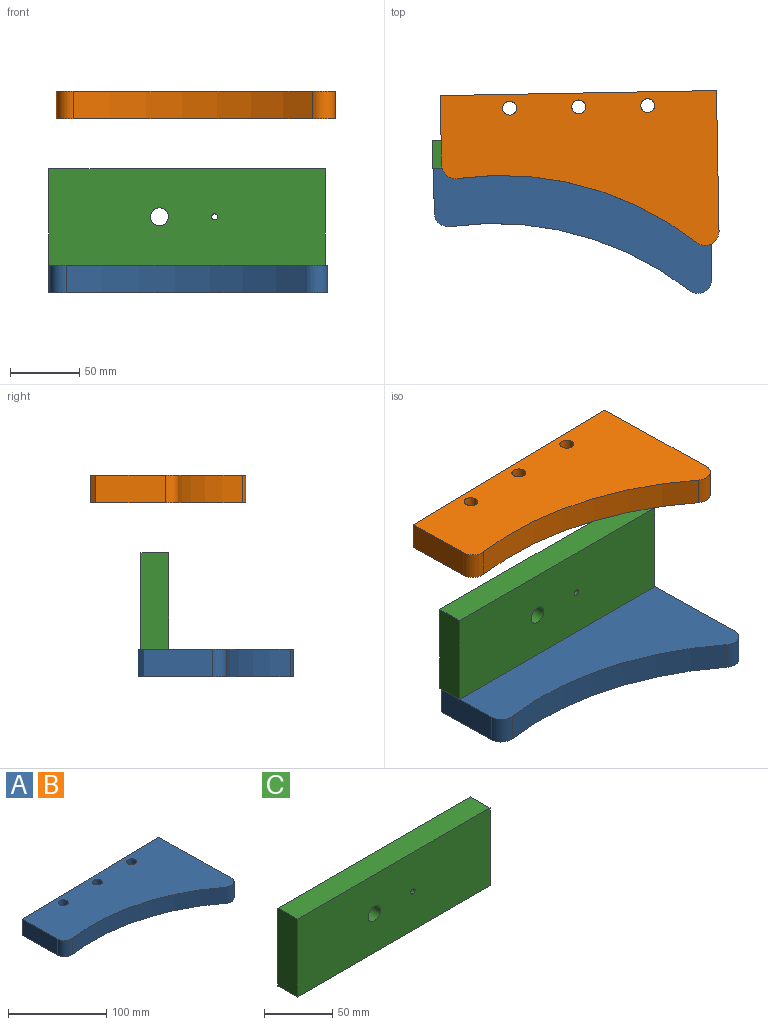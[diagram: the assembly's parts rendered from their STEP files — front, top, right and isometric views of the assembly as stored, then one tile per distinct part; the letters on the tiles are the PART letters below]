
ASSEMBLY  parts=3 mates=1
PART A: 11 faces, bbox 201.8x112.1x20 mm
  f0: plane 101.93x20mm, normal (1,0.02,0), area 2039mm2, adj f1,f7,f9,f10
  f1: plane 199.97x20mm, normal (-0.02,1,0), area 4000mm2, adj f0,f2,f9,f10
  f2: plane 50.28x20mm, normal (-1,-0.02,0), area 1005.8mm2, adj f1,f3,f9,f10
  f3: cylinder r=10mm len=20mm, axis (0,0,-1), area 338.6mm2, adj f2,f4,f9,f10
  f4: cylinder r=229.46mm len=173.36mm, axis (0,0,-1), area 3687.3mm2, adj f3,f7,f9,f10
  f5: cylinder r=5mm len=20mm, axis (0,0,-1), area 628.3mm2, adj f9,f10
  f6: cylinder r=5mm len=20mm, axis (0,0,-1), area 628.3mm2, adj f9,f10
  f7: cylinder r=10mm len=20mm, axis (0,0,-1), area 450.4mm2, adj f0,f4,f9,f10
  f8: cylinder r=5mm len=20mm, axis (0,0,-1), area 628.3mm2, adj f9,f10
  f9: plane 201.84x112.12mm, normal (0,0,1), area 14669.9mm2, adj f0,f1,f2,f3,f4,f5,f6,f7
  f10: plane 201.84x112.12mm, normal (0,0,-1), area 14669.9mm2, adj f0,f1,f2,f3,f4,f5,f6,f7
PART B: same geometry as A
PART C: 8 faces, bbox 200x20x70 mm
  f0: plane 200x20mm, normal (0,0,1), area 4000mm2, adj f1,f5,f6,f7
  f1: plane 70x20mm, normal (-1,0,0), area 1400mm2, adj f0,f2,f6,f7
  f2: plane 200x20mm, normal (0,0,-1), area 4000mm2, adj f1,f5,f6,f7
  f3: cylinder r=6.5mm len=20mm, axis (0,1,0), area 816.8mm2, adj f6,f7
  f4: cylinder r=2.25mm len=20mm, axis (0,1,0), area 282.7mm2, adj f6,f7
  f5: plane 70x20mm, normal (1,0,0), area 1400mm2, adj f0,f2,f6,f7
  f6: plane 200x70mm, normal (0,-1,0), area 13851.4mm2, adj f0,f1,f2,f3,f4,f5
  f7: plane 200x70mm, normal (0,1,0), area 13851.4mm2, adj f0,f1,f2,f3,f4,f5
PLACE A t=(2.92,-37.03,-51.57)mm
PLACE B t=(8.2,-2.48,74.46)mm
PLACE C t=(-47.58,71.13,22.6)mm
MATE fastened A.f9 <-> C.f2  axis (0,0,1) through (-39.21,71.13,-31.57)mm
